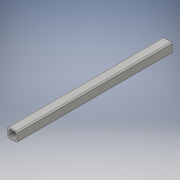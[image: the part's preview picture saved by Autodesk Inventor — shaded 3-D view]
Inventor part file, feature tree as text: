
AUTODESK INVENTOR PART (.ipt)
format: ipt  version: 2016 (Build 200138000, 138)  size: 113,664 bytes
history: native  units: in
note: dims shown in document units (in); Inventor stores cm internally (conversion verified against a paired STEP export)
features: extrude x1, sketch x1
ambient origin geometry x8: Origin, YZ Plane, XZ Plane, XY Plane, X Axis, Y Axis, Z Axis, Center Point
bodies: Solid1 (feature_tree)
feature tree (2):
  extrude  "Extrusion1"  Depth=1.0in
  sketch  "Sketch1"  dims[d0=1.0in d1=1.0in d2=0.125in d3=0.125in d4=16.0in d5=0.0in]
